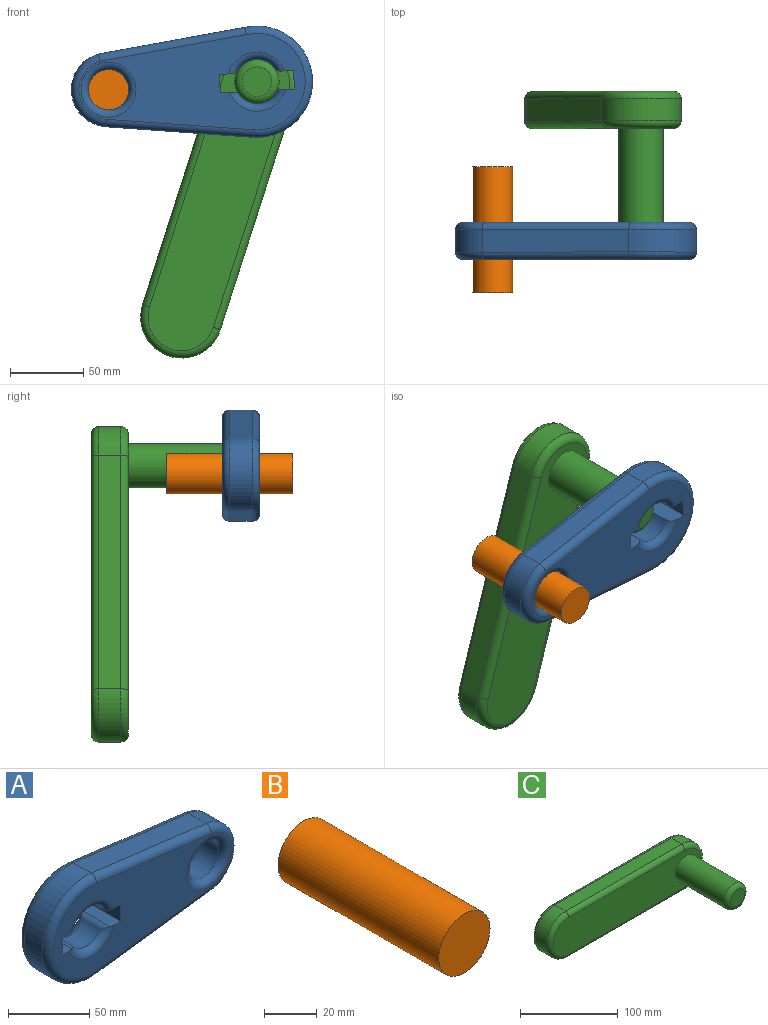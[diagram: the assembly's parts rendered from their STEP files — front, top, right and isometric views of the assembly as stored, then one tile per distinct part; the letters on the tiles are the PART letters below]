
ASSEMBLY  parts=3 mates=2
PART A: 31 faces, bbox 170.4x25.4x82.5 mm
  f0: cylinder r=15.15mm len=25.01mm, axis (0,1,0), area 448.2mm2, adj f23,f24,f25,f26
  f1: plane 25.43x8.74mm, normal (0,0,1), area 220.1mm2, adj f2,f13,f14,f24,f25,f26
  f2: plane 25.4x12.7mm, normal (1,0,0), area 322.6mm2, adj f1,f3,f13,f14
  f3: plane 25.4x11.64mm, normal (0,0,-1), area 283.7mm2, adj f2,f4,f13,f14,f28,f30
  f4: cylinder r=15.15mm len=27.52mm, axis (0,1,0), area 525.8mm2, adj f3,f5,f28,f30
  f5: plane 25.4x11.64mm, normal (0,0,-1), area 283.7mm2, adj f4,f6,f13,f14,f28,f30
  f6: plane 25.4x12.7mm, normal (-1,0,0), area 322.6mm2, adj f5,f12,f13,f14
  f7: plane 100.02x15.24mm, normal (0.12,0,0.99), area 1536.3mm2, adj f8,f11,f15,f19
  f8: cylinder r=38.1mm len=76.2mm, axis (0,1,0), area 1992.2mm2, adj f7,f9,f16,f20
  f9: plane 101.1x15.24mm, normal (0.13,0,-0.99), area 1553.1mm2, adj f8,f11,f18,f22
  f10: cylinder r=13.71mm len=27.42mm, axis (0,1,0), area 1313mm2, adj f27,f29
  f11: cylinder r=25.4mm len=49.95mm, axis (0,1,0), area 1079.7mm2, adj f7,f9,f17,f21
  f12: plane 25.43x8.74mm, normal (0,0,1), area 220.1mm2, adj f6,f13,f14,f23,f24,f25
  f13: plane 154.94x66.04mm, normal (0,-1,0), area 5279.9mm2, adj f1,f2,f3,f5,f6,f12,f15,f16
  f14: plane 154.94x66.04mm, normal (0,1,0), area 5279.9mm2, adj f1,f2,f3,f5,f6,f12,f19,f20
  f15: cylinder r=5.08mm len=100.65mm, axis (0.99,0,-0.12), area 804.4mm2, adj f7,f13,f16,f17
  f16: torus R=33.02mm, axis (0,-1,0), area 992.9mm2, adj f8,f13,f15,f18
  f17: torus R=20.32mm, axis (0,-1,0), area 523.5mm2, adj f11,f13,f15,f18
  f18: cylinder r=5.08mm len=101.84mm, axis (-0.99,0,-0.13), area 812.8mm2, adj f9,f13,f16,f17
  f19: cylinder r=5.08mm len=100.65mm, axis (-0.99,0,0.12), area 804.4mm2, adj f7,f14,f20,f21
  f20: torus R=33.02mm, axis (0,-1,0), area 992.9mm2, adj f8,f14,f19,f22
  f21: torus R=20.32mm, axis (0,-1,0), area 523.5mm2, adj f11,f14,f19,f22
  f22: cylinder r=5.08mm len=101.84mm, axis (0.99,0,0.13), area 812.8mm2, adj f9,f14,f20,f21
  f23: cylinder r=5.08mm len=24.23mm, axis (0,1,0), area 100.1mm2, adj f0,f12,f24,f25
  f24: torus R=20.23mm, axis (0,-1,0), area 312.5mm2, adj f0,f1,f12,f13,f23,f26
  f25: torus R=20.23mm, axis (0,-1,0), area 312.5mm2, adj f0,f1,f12,f14,f23,f26
  f26: cylinder r=5.08mm len=24.23mm, axis (0,1,0), area 100.1mm2, adj f0,f1,f24,f25
  f27: torus R=18.79mm, axis (0,-1,0), area 780mm2, adj f10,f14
  f28: torus R=20.23mm, axis (0,-1,0), area 322.2mm2, adj f3,f4,f5,f13
  f29: torus R=18.79mm, axis (0,-1,0), area 780mm2, adj f10,f13
  f30: torus R=20.23mm, axis (0,-1,0), area 322.2mm2, adj f3,f4,f5,f14
PART B: 3 faces, bbox 27.4x86.1x27.4 mm
  f0: cylinder r=13.72mm len=86.11mm, axis (0,1,0), area 7420.6mm2, adj f1,f2
  f1: plane 27.43x27.43mm, normal (0,-1,0), area 591mm2, adj f0
  f2: plane 27.43x27.43mm, normal (0,1,0), area 591mm2, adj f0
PART C: 17 faces, bbox 228.3x99.8x60.5 mm
  f0: cylinder r=27.94mm len=55.88mm, axis (0,1,0), area 1337.7mm2, adj f1,f3,f9,f12
  f1: plane 167.79x15.24mm, normal (0,0,-1), area 2557.1mm2, adj f0,f2,f11,f13
  f2: cylinder r=27.94mm len=55.88mm, axis (0,1,0), area 1337.7mm2, adj f1,f3,f10,f15
  f3: plane 167.79x15.24mm, normal (0,0,1), area 2557.1mm2, adj f0,f2,f8,f14
  f4: plane 213.51x45.72mm, normal (0,-1,0), area 8591.9mm2, adj f6,f12,f13,f14,f15
  f5: plane 213.51x45.72mm, normal (0,1,0), area 9313mm2, adj f8,f9,f10,f11
  f6: cylinder r=15.15mm len=69.34mm, axis (0,1,0), area 6601.2mm2, adj f4,f16
  f7: plane 20.14x20.14mm, normal (0,-1,0), area 318.6mm2, adj f16
  f8: cylinder r=5.08mm len=167.79mm, axis (-1,0,0), area 1338.9mm2, adj f3,f5,f9,f10
  f9: torus R=22.86mm, axis (0,-1,0), area 654.1mm2, adj f0,f5,f8,f11
  f10: torus R=22.86mm, axis (0,-1,0), area 654.1mm2, adj f2,f5,f8,f11
  f11: cylinder r=5.08mm len=167.79mm, axis (1,0,0), area 1338.9mm2, adj f1,f5,f9,f10
  f12: torus R=22.86mm, axis (0,-1,0), area 654.1mm2, adj f0,f4,f13,f14
  f13: cylinder r=5.08mm len=167.79mm, axis (-1,0,0), area 1338.9mm2, adj f1,f4,f12,f15
  f14: cylinder r=5.08mm len=167.79mm, axis (1,0,0), area 1338.9mm2, adj f3,f4,f12,f15
  f15: torus R=22.86mm, axis (0,-1,0), area 654.1mm2, adj f2,f4,f13,f14
  f16: torus R=10.07mm, axis (0,-1,0), area 667.1mm2, adj f6,f7
PLACE A rot(axis=(0,1,0),176.9deg) t=(238.61,266.47,238.92)mm
PLACE B t=(137.15,304.44,233.46)mm fixed
PLACE C rot(axis=(0,-1,0),72.2deg) t=(219.62,356.13,179.65)mm
MATE revolute C.f6 <-> A.f0  axis (0,1,0) through (238.61,261.39,238.92)mm
MATE revolute B.f0 <-> A.f10  axis (0,1,0) through (137.15,261.39,233.46)mm
